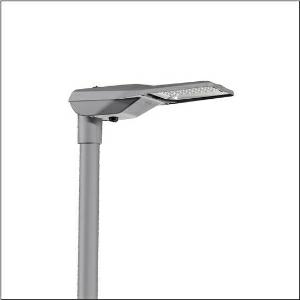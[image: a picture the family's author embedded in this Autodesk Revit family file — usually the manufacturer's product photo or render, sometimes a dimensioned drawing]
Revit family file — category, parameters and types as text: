
# Revit family: streetlight_sl_21_iq_mini___st1_0a_5xe2d51y08jb_5dfa
name_source: partatom
category: Lighting Fixtures
units: mm (PartAtom-declared; Revit-internal decimal feet)

## family parameters
Cut with Voids When Loaded = No
Host = Face
Light Source = No
Part Type = Normal
Room Calculation Point = No
Round Connector Dimension = Use Diameter
Shared = No

## types (1)
- --- (1 x LED, 9850 lm, 72.5 W, 3000K)
    Apparent Load = 73 VA
    CIE Flux Codes = 40 73 97 100 100
    Color Rendering = 80
    Color Temperature = 3000K
    Default Elevation = 1800 mm
    Description = Streetlight SL 21 iQ mini, mast luminaire, primary light control with lens, of PMMA, primary optical cover: cover, of toughened safety glass, transparent, light distribution: ST1.0a, light emission: direct distribution, primary light characteristic: asymmetric, installation type: post-top, side-entry, LED, High Power LED, rated luminous flux: 9.850lm, luminous efficacy: 136lm/W, light colour: 830, colour temperature: 3000K, control gear: iQ-Street Remote, D4i with power reduction, control: pre-setting: logarithmic dimming characteristic, Street-Remote, Auto-Match, Temp-Guard, Lumen-Switch, Night-Set, Smart-Wire, Light-Fading, Desk-Remote (wireless, voltage-free reading and setting of iQ features in the workshop via application-optimized NFC function/RFID function), optimised constant luminous flux control (CLO 2.0), mains connection: 220..240V, AC, 50/60Hz, start of lifetime: 73W, end of service life: 76W, reduction: 33W, luminaire housing, of diecast aluminium, powder-coated, SITECO metallic grey (DB 702S), corrosivity category C5 high according to DIN EN ISO 12944, please order mast flange separately, inclination adjustable: 0°, 5°, 10°, 15°, sealing non-destructively replaceable, multi-level sealing system, length: 628mm, width: 235mm, height: 110mm, mast flange for spigot size: 42mm (side-entry): 5XC10008XM4, 60/48mm (side-entry/post-top): 5XC10108XM2, 76/60mm (side-entry/post-top): 5XC10108XM1, mounting height: 4..8m, Smart Interface below and above, protection rating (complete): IP66, insulation class (complete): insulation class II (safety insulation), certification: CE, ENEC, ENEC+, VDE, impact resistance: IK10, permissible operating ambient temperature for outdoor applications: -40..+50°C, standard-compliant lighting for roads and squares, packaging unit: 1 piece

Light Distribution: ST1.0a
    Height = 110 mm
    Lamp = 1 x LED
    Lamp Light Flux = 9850 lm
    Lamp Power = 72.5 W
    Lamp count = 1
    Length = 625 mm
    Luminous efficacy = 136 lm/W
    Manufacturer = Siteco
    ModVariant = No
    Model = 5XE2D51Y08JB
    Number of Poles = 1
    OnlyDefault = Yes
    Power Factor = 1
    Product Name = Streetlight SL 21 iQ mini | ST1.0a
    Product group = mast luminaire | pylon top
    ProductGroupID = 6100
    Protection Class = Protection class II
    Protection Degree = IP 66
    RLX_Detail_Level = 1
    RLX_Emergency_Light_Flux = 0 lm
    RLX_Emergency_Type = 0
    RLX_Emergency_Type_DB = No
    RlxData = <blob elided: 92685 chars, md5=ec6db3e7>
    Socket = socket
    Standby Power = 0 W
    System Light Flux = 9850 lm
    System Power = 73 W
    Type Comments = factory setting: luminous flux: 100 % | dim-lin: 254 | 755 mA
    Type Image = l_1003514.jpg
    URL = http://relux.com
    VarID = @adj_114157
    Voltage = 0 V
    Weight = 0.00 kg
    Width = 234 mm

## geometry (parser evidence)
native form markers: Blend x4, Sweep x13
no freeform markers — native parametric forms only
